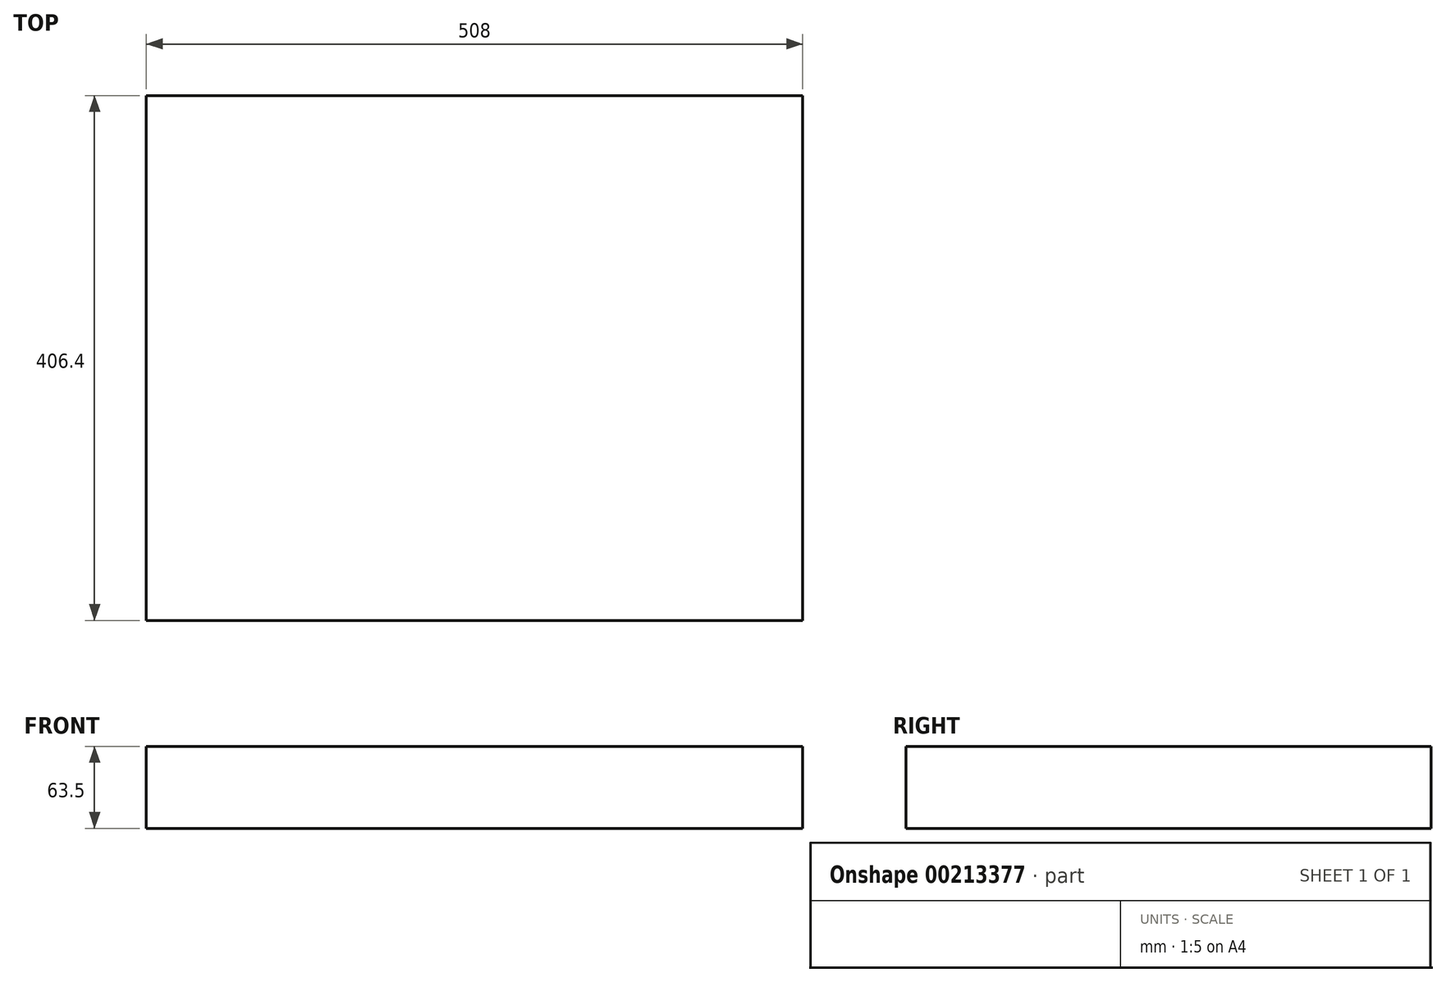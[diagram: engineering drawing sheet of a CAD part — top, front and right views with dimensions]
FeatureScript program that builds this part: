
annotation { "Feature Type Name" : "Feature", "Feature Type Description" : "" }
export const myFeature = defineFeature(function(context is Context, id is Id, definition is map)
    precondition{}
    {
        {
            var Q0;
            Q0=qCreatedBy(makeId("Top.planeOp"),FACE);
            var sketch = newSketch(context, id + "F0", { "sketchPlane" : qUnion([Q0])});
            skLineSegment(sketch, "E0.bottom", {"start": v(-238.51, 268.12) * mm, "end": v(269.49, 268.12) * mm});
            skLineSegment(sketch, "E0.top", {"start": v(-238.51, -138.28) * mm, "end": v(269.49, -138.28) * mm});
            skLineSegment(sketch, "E0.left", {"start": v(-238.51, 268.12) * mm, "end": v(-238.51, -138.28) * mm});
            skLineSegment(sketch, "E0.right", {"start": v(269.49, 268.12) * mm, "end": v(269.49, -138.28) * mm});
            skSolve(sketch);
        }
        {
            var Q0;
            Q0=makeQuery(id+"F0.imprint","IMPRINT",FACE,{"disambiguationData":[TD([[makeQuery(id+"F0.imprint","IMPRINT",EDGE,{"derivedFrom":sQuery(id+"F0.wireOp",EDGE,"E0.bottom")}),-1.0]])]});
            extrude(context, id + "F1", {"entities" : qUnion([Q0]), "depth" : 63.5 * mm});
        }
    });
